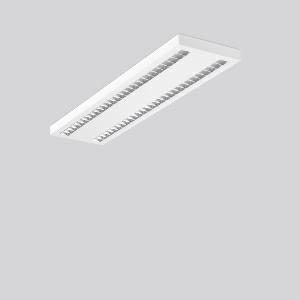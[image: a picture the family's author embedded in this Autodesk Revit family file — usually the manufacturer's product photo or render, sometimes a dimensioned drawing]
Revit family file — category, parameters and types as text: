
# Revit family: sonis_901691_002_1_a0a0
name_source: partatom
category: Lighting Fixtures
units: mm (PartAtom-declared; Revit-internal decimal feet)

## family parameters
Cut with Voids When Loaded = No
Host = Face
Light Source = No
Part Type = Normal
Room Calculation Point = No
Round Connector Dimension = Use Diameter
Shared = No

## types (1)
- Sonis (1 x LED Modul 840, 6500 lm, 4000)
    Apparent Load = 50 VA
    CIE Flux Codes = 83 100 100 100 100
    Color Rendering = 80
    Color Temperature = 4000
    Default Elevation = 1800 mm
    Description = Series: SONIS
High-efficiency LED louvre surface-mounted luminaire. Housing: metal, powder-coated. Alea optical system: Reflector structure (ABS, Aluminium-coated, highly polished) with integrated diffuser made of non-yellowing plastic (PMMA) opal for glare-free light at the workstation. Narrow beam, brilliant luminous effect. Suitable for Ceiling mounting. Driver integrated. Perfect for office areas (RUG < 19) and environments with computer screens in accordance with EN 12464-1. 
Colour: white
Length: 1202 mm
Width: 302 mm
Height: 47 mm
Lamp: LED
Socket: without socket
Colour temperature: 4000K
Colour rendering index (CRI): 80
System power: 50 W
Rated luminous flux: 6500 lm
Luminous efficiency: 130 lm/W
Control gear: Regulated power supply
Protection class: I
Type of protection: IP 20
    Height = 33 mm
    Lamp = 1 x LED Modul 840
    Lamp Light Flux = 6500 lm
    Lamp count = 1
    Length = 1202 mm
    Lifetime = 50000 h
    Luminous efficacy = 130 lm/W
    Manufacturer = RZB
    ModVariant = No
    Model = 901691.002.1
    Mounting Place = Ceiling
    Mounting Type = Surface mounted
    Number of Poles = 1
    OnlyDefault = Yes
    Power Factor = 1
    Product Name = Sonis
    Product group = Surface mounted modular luminaires
    ProductGroupID = 306
    Protection Class = Protection class I
    Protection Degree = IP 20
    RLX_Detail_Level = 1
    RLX_Emergency_Light_Flux = 0 lm
    RLX_Emergency_Type = 0
    RLX_Emergency_Type_DB = No
    RlxData = <blob elided: 24769 chars, md5=d432e55f>
    Socket = socket
    Standby Power = 0 W
    System Light Flux = 6500 lm
    System Power = 50 W
    Type Comments = Product without accessories
    Type Image = 901650.002.jpg
    URL = http://relux.com
    VarID = ---
    Voltage = 230 V
    Voltage Range = 220-240 V
    Weight = 0.00 kg
    Width = 302 mm

## geometry (parser evidence)
native form markers: Blend x4, Sweep x11
no freeform markers — native parametric forms only
